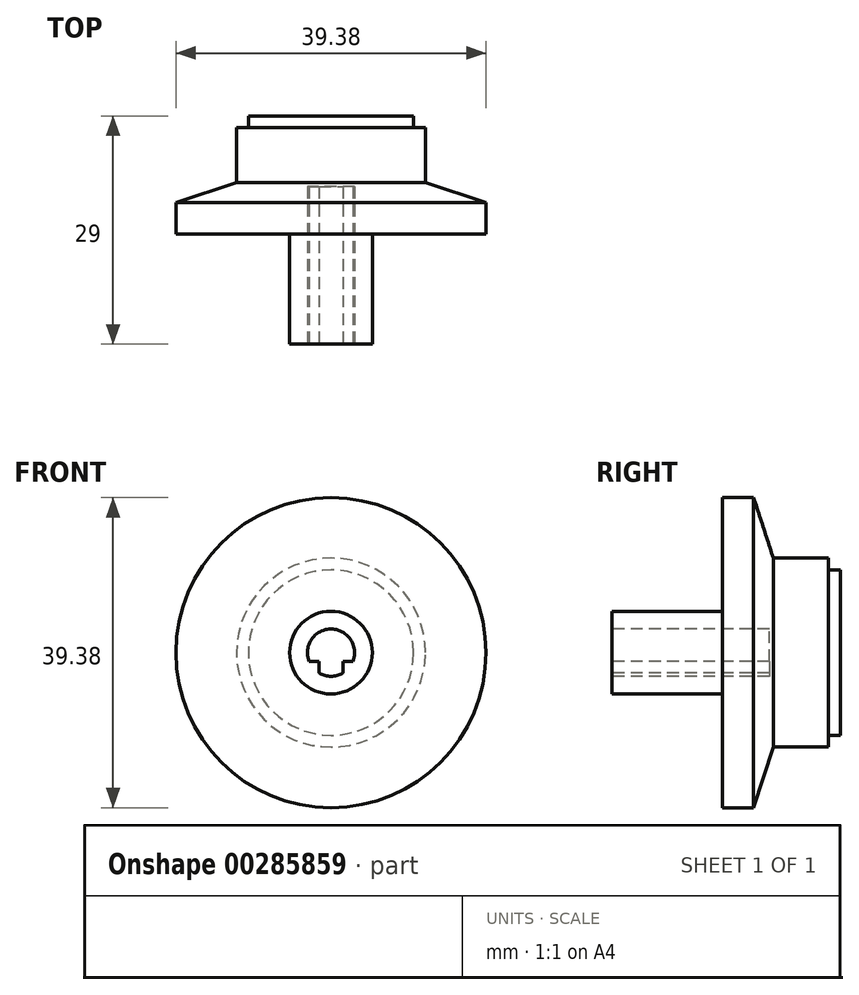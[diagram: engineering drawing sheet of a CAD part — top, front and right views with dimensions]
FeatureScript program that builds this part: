
annotation { "Feature Type Name" : "Feature", "Feature Type Description" : "" }
export const myFeature = defineFeature(function(context is Context, id is Id, definition is map)
    precondition{}
    {
        {
            var Q0;
            Q0=qCreatedBy(makeId("Top.planeOp"),FACE);
            var sketch = newSketch(context, id + "F0", { "sketchPlane" : qUnion([Q0])});
            skLineSegment(sketch, "E0", {"start": v(5.25, -2.5) * mm, "end": v(5.25, -16.5) * mm});
            skLineSegment(sketch, "E1", {"start": v(-5.25, -16.5) * mm, "end": v(0, -16.5) * mm, "construction": true});
            skLineSegment(sketch, "E2", {"start": v(0, 0) * mm, "end": v(0, -29.48) * mm, "construction": true});
            skLineSegment(sketch, "E3", {"start": v(0, -16.5) * mm, "end": v(0, 12.5) * mm});
            skLineSegment(sketch, "E4", {"start": v(0, -16.5) * mm, "end": v(5.25, -16.5) * mm});
            skLineSegment(sketch, "E5", {"start": v(0, 12.5) * mm, "end": v(10.5, 12.5) * mm});
            skLineSegment(sketch, "E6", {"start": v(10.5, 12.5) * mm, "end": v(10.5, 11) * mm});
            skLineSegment(sketch, "E7", {"start": v(10.5, 11) * mm, "end": v(12, 11) * mm});
            skLineSegment(sketch, "E8", {"start": v(12, 11) * mm, "end": v(12, 4) * mm});
            skLineSegment(sketch, "E9", {"start": v(19.7, -2.5) * mm, "end": v(19.7, 1.5) * mm});
            skLineSegment(sketch, "E10", {"start": v(19.7, 1.5) * mm, "end": v(12, 4) * mm});
            skLineSegment(sketch, "E11", {"start": v(5.25, -2.5) * mm, "end": v(19.7, -2.5) * mm});
            skSolve(sketch);
        }
        {
            var Q0;
            Q0 = qSketchRegion(id + "F0", true);
            var Q1;
            Q1=sQuery(id+"F0.wireOp",EDGE,"E2");
            revolve(context, id + "F1", {"entities" : qUnion([Q0]), "axis" : qUnion([Q1]), "revolveType" : RevolveType.FULL});
        }
        {
            var Q0;
            Q0=makeQuery(id+"F1.opRevolve","SWEPT_FACE",FACE,{"disambiguationData":[OSD([sQuery(id+"F0.wireOp",EDGE,"E4")])]});
            var sketch = newSketch(context, id + "F2", { "sketchPlane" : qUnion([Q0])});
            skArc(sketch, "E12", {"start": v(-1.5, -2.6) * mm, "mid": v(0, -3) * mm, "end": v(1.5, -2.6) * mm});
            skLineSegment(sketch, "E13", {"start": v(-2.8, -1.1) * mm, "end": v(-1.5, -1.1) * mm});
            skLineSegment(sketch, "E14", {"start": v(-1.5, -1.1) * mm, "end": v(-1.5, -2.6) * mm});
            skLineSegment(sketch, "E15", {"start": v(2.8, -1.1) * mm, "end": v(1.5, -1.1) * mm});
            skLineSegment(sketch, "E16", {"start": v(1.5, -1.1) * mm, "end": v(1.5, -2.6) * mm});
            skArc(sketch, "E17.trimOffspring", {"start": v(2.8, -1.1) * mm, "mid": v(0, 3) * mm, "end": v(-2.8, -1.1) * mm});
            skSolve(sketch);
        }
        {
            var Q0;
            Q0 = qSketchRegion(id + "F2", true);
            extrude(context, id + "F3", {"entities" : qUnion([Q0]), "operationType" : NewBodyOperationType.REMOVE, "oppositeDirection" : true, "depth" : 20 * mm});
        }
    });
